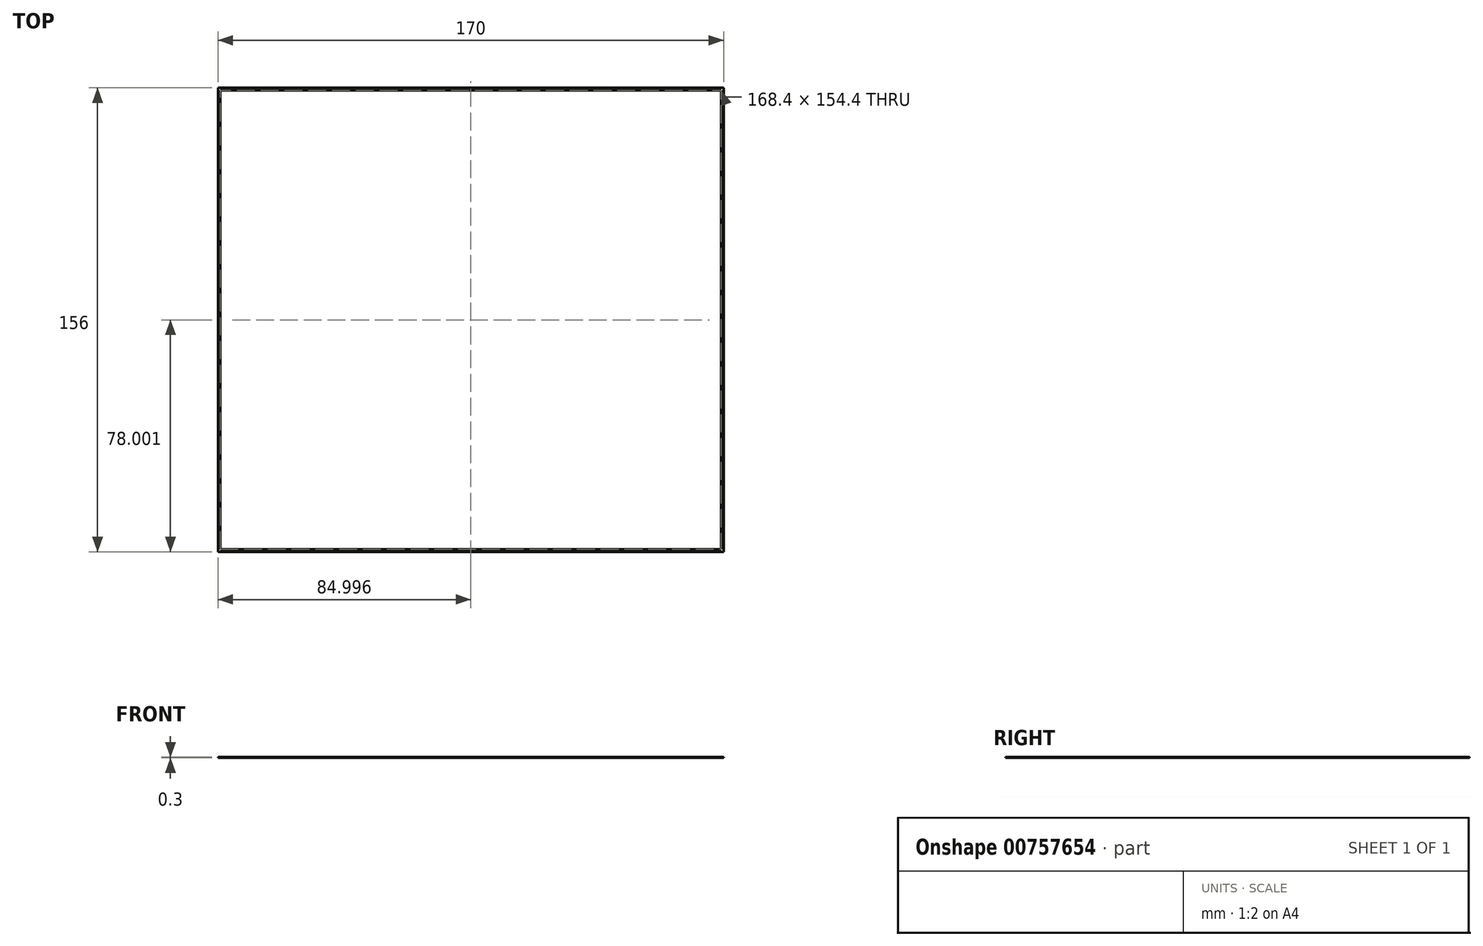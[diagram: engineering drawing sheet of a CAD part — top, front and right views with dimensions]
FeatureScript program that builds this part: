
annotation { "Feature Type Name" : "Feature", "Feature Type Description" : "" }
export const myFeature = defineFeature(function(context is Context, id is Id, definition is map)
    precondition{}
    {
        {
            var Q0;
            Q0=qCreatedBy(makeId("Top.planeOp"),FACE);
            var sketch = newSketch(context, id + "F0", { "sketchPlane" : qUnion([Q0])});
            skLineSegment(sketch, "E0.bottom", {"start": v(-95.98, 66.3) * mm, "end": v(74.02, 66.3) * mm});
            skLineSegment(sketch, "E0.top", {"start": v(-95.98, -89.7) * mm, "end": v(74.02, -89.7) * mm});
            skLineSegment(sketch, "E0.left", {"start": v(-95.98, 66.3) * mm, "end": v(-95.98, -89.7) * mm});
            skLineSegment(sketch, "E0.right", {"start": v(74.02, 66.3) * mm, "end": v(74.02, -89.7) * mm});
            skLineSegment(sketch, "E1.0", {"start": v(-95.18, 65.5) * mm, "end": v(-95.18, -88.9) * mm});
            skLineSegment(sketch, "E1.1", {"start": v(-95.18, 65.5) * mm, "end": v(73.22, 65.5) * mm});
            skLineSegment(sketch, "E1.2", {"start": v(73.22, 65.5) * mm, "end": v(73.22, -88.9) * mm});
            skLineSegment(sketch, "E1.3", {"start": v(-95.18, -88.9) * mm, "end": v(73.22, -88.9) * mm});
            skSolve(sketch);
        }
        {
            var Q0;
            Q0=makeQuery(id+"F0.imprint","IMPRINT",FACE,{"disambiguationData":[TD([[makeQuery(id+"F0.imprint","IMPRINT",EDGE,{"derivedFrom":sQuery(id+"F0.wireOp",EDGE,"E0.bottom")}),-1.0]])]});
            extrude(context, id + "F1", {"entities" : qUnion([Q0]), "depth" : 0.3 * mm, "offsetDistance" : 25 * mm});
        }
    });
